# Revit family: 5865017282
name_source: partatom
category: Plumbing Fixtures
units: mm (PartAtom-declared; Revit-internal decimal feet)

## family parameters
Always vertical = Yes
Cut with Voids When Loaded = No
OmniClass Number = 23.45.55.00
OmniClass Title = Sanitary Faucets, Wastes
Part Type = Normal
Room Calculation Point = No
Round Connector Dimension = Use Diameter
Shared = No
Work Plane-Based = No

## types (1)
- 5865017282 Shower system, 6 V, Bluetooth
    2D/3D/BIM Files URL = http://static.hansa.com
    3D View = https://static.hansa.com
    Additional Features = protected against back-flow in domestic use (according to DIN EN 1717)
    Advanced Features = Safety glass;Software settings adjustable via App
    Ambience photo = http://static.hansa.com
    AssetType = Fixed
    BIMObjectName = 5865017282
    Backflow Prevention EN1717 = EB
    Battery = AA 1.5 V Lithium x 4
    Bluetooth = 4.x (D034445)
    BodyMaterial = Brass
    Brand = HANSA
    Catalog Drawing URL = http://static.hansa.com
    Category = Shower solutions
    CloseOffRating = 0
    Color = Chrome/White
    Connection = Ball eccentric coupling(s)
    Connection Size = G1/2
    Default Elevation = 0 mm  [stored 0 ft]
    Dimension Drawing URL = http://static.hansa.com
    Diverter = Turn operated diverter;Integrated into flow control handle
    DurationUnit = Year
    EAN Number = 4057304007842
    EMC Directive = Radio Equipment Directive 2014/53/EU , 
Low Voltage Directive 2014/35/EU , 
EMC Directive 2014/30/EU , 
RoHS Directive 2011/65/EU
    EN Standard = EN 1111, EN 1112, EN 1113, EN 15091, ETSI EN 301 489-1 V1.9.2 , 
ETSI EN 300 328 v2.2.2 , 
EN 61000-6-1:2007 , 
EN 61000-6-3:2007+A1:2011+AC:2012 , 
EN 60335-1:2012+A11+A13+A1+A14+A2+A15:2021, Part 19.11.4
    ETIM Class Number = EC011329 Shower mixing tap
    Electronic Parts = Solenoid valve;External control unit;Light indicated function(s);Low battery indicator
    FDV Document URL = http://www.hansa.com
    FaucetMainMaterial = Brass
    FaucetNominalDepth = 509 mm  [stored 1.66995 ft]
    FaucetNominalHeight = 1167 mm
    FaucetNominalWidth = 371 mm
    Features = Thermostatic;Bluetooth®;Battery-operated
    Finish = Polished
    Flow Drawing URL = http://static.hansa.com
    Flow Rate At 300kPa = 0.0 L/s
    FlowCoefficient = 0
    Group = Shower system
    Hand Shower Size = 110x120 mm
    HandShowerNominalDepth = 103 mm
    HandShowerNominalHeight = 377 mm
    HandShowerNominalWidth = 124 mm  [stored 0.406824 ft]
    IfcExportAs = IfcValveType
    IfcExportType = FAUCET
    Installation Type = Wall mounted
    Installation Width = CC150± 15 mm
    Installation and Maintenance Guide URL = http://static.hansa.com
    Interactive AR View URL = https://static.hansa.com
    Lever Handle = Temperature control handle;Flow control handle
    Lifestyle photo = http://static.hansa.com
    Manufacturer = HANSA
    ManufacturerName = HANSA
    ManufacturerURL = http://www.hansa.com
    Market = Austria;Belgium;Czech Republic;Germany;Spain;France;International;Italy;Netherlands;Slovakia
    Material = Brass
    Max. Hot Water Supply = 70 °C
    Mechanical Parts = Thermostatic cartridge for automatic temperature control;Non-return valve(s)
    Mobile Product Information URL = http://mpi.hansa.com
    Model = 5865017282 Shower system, 6 V, Bluetooth
    ModelReference = 5865017282
    NBSDescription = Shower mixers
    NBSReference = 45-35-70/335
    Name = 5865017282 Shower system, 6 V, Bluetooth
    Name_en = 5865017282 Shower system, 6 V, Bluetooth
    Noise Class = I (ISO 3822) Oras lab.
    Operating Voltage = 6 V
    Over Head Shower Size = 360x220 mm
    Pressure Loss With Flow 02ls = 210000.0 Pa
    Product Code = 5865017282
    Product Family = HANSAEMOTION Wellfit
    Product Image URL = http://static.hansa.com
    Product URL = http://static.hansa.com
    ProductInformation = Thermostatic rain shower faucet with easy-grip handles and a spout
    Protection Class = IP 55
    Sales Package dimensions (LxWxH) = 1017 x 230 x 144
    Shape = Sculptured
    Shower Parts = Hand shower;Shower holder;Shower hose (1750 mm);Overhead shower;Rotatable ball joint connection
    Shower Spray = Pulsating;Intense;Sensitive
    Shower Spray Number = 3 shower sprays
    Size = Faucet: 370x510x1165 mm / Hand shower: 125x105x380 mm
    Spare-Part Information URL = http://static.hansa.com
    Spout Projection = 401 mm
    Surface treatment = Chrome/White
    Technical DataSheet URL = http://www.hansa.com
    Temperature = Thermostatic safety stop at 38°C;THERMO COOL
    Temperature Adjustments = Safety stop against scalding at 38°C;The housing of the fittings conducts minimal heat
    UNSPSC Class Number = 30181805 Combination fixed and hand held shower head
    URL Declaration Of Performance (DOP) = http://static.hansa.com
    URL Declaration of Asbestos = http://static.hansa.com
    URL Declaration of Conformity = http://static.hansa.com
    URL Declaration of SCIP = http://static.hansa.com
    URL EU Packaging Declaration = http://static.hansa.com
    URL EcoLabel Declaration = http://static.hansa.com
    URL REACH = http://static.hansa.com
    URL UN38.3 = http://static.hansa.com
    URL WEEE = http://static.hansa.com
    Uniclass2 = Pr_40_30_96_81
    Uniclass2015Description = Shower thermostatic water supply sets
    Uniclass2015Reference = Pr_40_20_87_81
    Version = 1
    VersionDate = 01/06/2023
    Warranty Information URL = http://warranty.hansa.com
    WarrantyDescription = http://warranty.hansa.com
    WarrantyDurationUnit = Year
    Working Pressure = 100 - 1000 kPa

note: [stored X ft] marks values corroborated as IEEE doubles in the binary element streams (Revit-internal decimal feet)

## geometry (parser evidence)
native form markers: Sweep x6
no freeform markers — native parametric forms only
